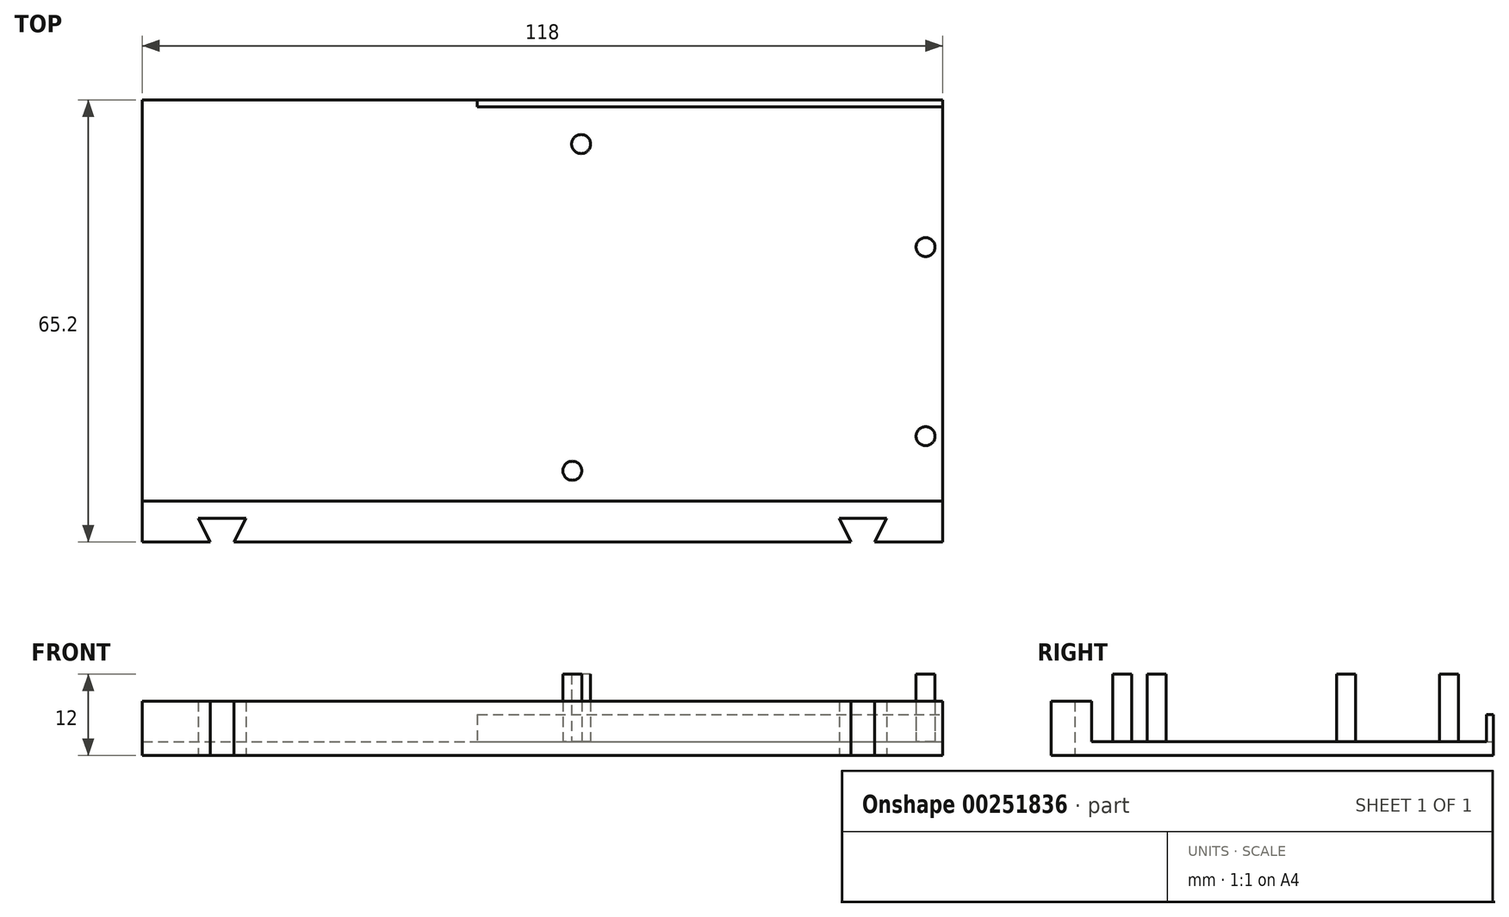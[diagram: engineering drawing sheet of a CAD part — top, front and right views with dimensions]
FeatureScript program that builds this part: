
annotation { "Feature Type Name" : "Feature", "Feature Type Description" : "" }
export const myFeature = defineFeature(function(context is Context, id is Id, definition is map)
    precondition{}
    {
        {
            var Q0;
            Q0=qCreatedBy(makeId("Top.planeOp"),FACE);
            var sketch = newSketch(context, id + "F0", { "sketchPlane" : qUnion([Q0])});
            skLineSegment(sketch, "E0", {"start": v(-10, 20) * mm, "end": v(-10, 0) * mm, "construction": true});
            skLineSegment(sketch, "E1", {"start": v(-10, 0) * mm, "end": v(-10, -10) * mm, "construction": true});
            skLineSegment(sketch, "E2", {"start": v(-10, -10) * mm, "end": v(0, -10) * mm, "construction": true});
            skLineSegment(sketch, "E3", {"start": v(0, -10) * mm, "end": v(100, -10) * mm, "construction": true});
            skLineSegment(sketch, "E4.bottom", {"start": v(100, 73.2) * mm, "end": v(168.6, 73.2) * mm});
            skLineSegment(sketch, "E4.top", {"start": v(100, 20) * mm, "end": v(168.6, 20) * mm});
            skLineSegment(sketch, "E4.left", {"start": v(100, 73.2) * mm, "end": v(100, 20) * mm});
            skLineSegment(sketch, "E4.right", {"start": v(168.6, 73.2) * mm, "end": v(168.6, 20) * mm});
            skLineSegment(sketch, "E5", {"start": v(115.3, -10) * mm, "end": v(166.1, -10) * mm, "construction": true});
            skLineSegment(sketch, "E6", {"start": v(-10, 22.5) * mm, "end": v(-10, 27.6) * mm, "construction": true});
            skLineSegment(sketch, "E7", {"start": v(-10, 27.6) * mm, "end": v(-10, 55.5) * mm, "construction": true});
            skCircle(sketch, "E8", {"center": v(-10, -10) * mm, "radius": 1.4 * mm, "construction": true});
            skCircle(sketch, "E9", {"center": v(114, 22.5) * mm, "radius": 1.4 * mm});
            skCircle(sketch, "E10", {"center": v(115.3, 70.7) * mm, "radius": 1.4 * mm});
            skCircle(sketch, "E11", {"center": v(166.1, 27.6) * mm, "radius": 1.4 * mm});
            skCircle(sketch, "E12", {"center": v(166.1, 55.5) * mm, "radius": 1.4 * mm});
            skLineSegment(sketch, "E13", {"start": v(-10, 55.5) * mm, "end": v(-10, 70.7) * mm, "construction": true});
            skLineSegment(sketch, "E14", {"start": v(115.3, -10) * mm, "end": v(114, -10) * mm, "construction": true});
            skLineSegment(sketch, "E15", {"start": v(114, -10) * mm, "end": v(100, -10) * mm, "construction": true});
            skLineSegment(sketch, "E16", {"start": v(166.1, -10) * mm, "end": v(168.6, -10) * mm, "construction": true});
            skLineSegment(sketch, "E17", {"start": v(-10, 70.7) * mm, "end": v(-10, 73.2) * mm, "construction": true});
            skLineSegment(sketch, "E18", {"start": v(-10, 22.5) * mm, "end": v(-10, 20) * mm, "construction": true});
            skLineSegment(sketch, "E19", {"start": v(100, 73.2) * mm, "end": v(100, 76.2) * mm});
            skLineSegment(sketch, "E20", {"start": v(100, 76.2) * mm, "end": v(168.6, 76.2) * mm});
            skLineSegment(sketch, "E21", {"start": v(168.6, 76.2) * mm, "end": v(168.6, 73.2) * mm});
            skLineSegment(sketch, "E22", {"start": v(100, 76.2) * mm, "end": v(100, 77.2) * mm});
            skLineSegment(sketch, "E23", {"start": v(100, 77.2) * mm, "end": v(168.6, 77.2) * mm});
            skLineSegment(sketch, "E24", {"start": v(168.6, 77.2) * mm, "end": v(168.6, 76.2) * mm});
            skLineSegment(sketch, "E25", {"start": v(62.35, 15.5) * mm, "end": v(62.35, 12) * mm, "construction": true});
            skLineSegment(sketch, "E26", {"start": v(62.35, 15.5) * mm, "end": v(58.85, 15.5) * mm});
            skLineSegment(sketch, "E27", {"start": v(65.85, 15.5) * mm, "end": v(62.35, 15.5) * mm});
            skLineSegment(sketch, "E28", {"start": v(60.6, 12) * mm, "end": v(64.1, 12) * mm, "construction": true});
            skLineSegment(sketch, "E29", {"start": v(58.85, 15.5) * mm, "end": v(60.6, 12) * mm});
            skLineSegment(sketch, "E30", {"start": v(65.85, 15.5) * mm, "end": v(64.1, 12) * mm});
            skLineSegment(sketch, "E31", {"start": v(60.6, 12) * mm, "end": v(50.6, 12) * mm});
            skLineSegment(sketch, "E32", {"start": v(50.6, 12) * mm, "end": v(50.6, 18) * mm});
            skLineSegment(sketch, "E33", {"start": v(156.85, 15.5) * mm, "end": v(156.85, 12) * mm, "construction": true});
            skLineSegment(sketch, "E34", {"start": v(156.85, 15.5) * mm, "end": v(153.35, 15.5) * mm});
            skLineSegment(sketch, "E35", {"start": v(160.35, 15.5) * mm, "end": v(156.85, 15.5) * mm});
            skLineSegment(sketch, "E36", {"start": v(155.1, 12) * mm, "end": v(158.6, 12) * mm, "construction": true});
            skLineSegment(sketch, "E37", {"start": v(153.35, 15.5) * mm, "end": v(155.1, 12) * mm});
            skLineSegment(sketch, "E38", {"start": v(160.35, 15.5) * mm, "end": v(158.6, 12) * mm});
            skLineSegment(sketch, "E39", {"start": v(64.1, 12) * mm, "end": v(155.1, 12) * mm});
            skLineSegment(sketch, "E40", {"start": v(158.6, 12) * mm, "end": v(168.6, 12) * mm});
            skLineSegment(sketch, "E41", {"start": v(168.6, 12) * mm, "end": v(168.6, 18) * mm});
            skLineSegment(sketch, "E42", {"start": v(50.6, 18) * mm, "end": v(168.6, 18) * mm});
            skLineSegment(sketch, "E43", {"start": v(50.6, 18) * mm, "end": v(50.6, 20) * mm});
            skLineSegment(sketch, "E44", {"start": v(50.6, 20) * mm, "end": v(168.6, 20) * mm});
            skLineSegment(sketch, "E45", {"start": v(168.6, 20) * mm, "end": v(168.6, 18) * mm});
            skLineSegment(sketch, "E46", {"start": v(50.6, 20) * mm, "end": v(50.6, 77.2) * mm});
            skLineSegment(sketch, "E47", {"start": v(50.6, 77.2) * mm, "end": v(100, 77.2) * mm});
            skSolve(sketch);
        }
        {
            var Q0;
            Q0=makeQuery(id+"F0.imprint","IMPRINT",FACE,{"disambiguationData":[TD([[makeQuery(id+"F0.imprint","IMPRINT",EDGE,{"derivedFrom":sQuery(id+"F0.wireOp",EDGE,"E4.bottom")}),-1.0]])]});
            var Q1;
            Q1=makeQuery(id+"F0.imprint","IMPRINT",FACE,{"disambiguationData":[TD([[makeQuery(id+"F0.imprint","IMPRINT",EDGE,{"derivedFrom":sQuery(id+"F0.wireOp",EDGE,"E4.bottom")}),1.0]])]});
            var Q2;
            Q2=makeQuery(id+"F0.imprint","IMPRINT",FACE,{"disambiguationData":[TD([[makeQuery(id+"F0.imprint","IMPRINT",EDGE,{"derivedFrom":sQuery(id+"F0.wireOp",EDGE,"E42")}),1.0]])]});
            var Q3;
            {var subQ1=sQuery(id+"F0.wireOp",EDGE,"E4.left");Q3=makeQuery(id+"F0.imprint","IMPRINT",FACE,{"disambiguationData":[TD([[makeQuery(id+"F0.imprint","IMPRINT",EDGE,{"derivedFrom":subQ1}),-1.0]])]});}
            extrude(context, id + "F1", {"entities" : qUnion([Q0, Q1, Q2, Q3]), "depth" : 2 * mm});
        }
        {
            var Q0;
            Q0=makeQuery(id+"F0.imprint","IMPRINT",FACE,{"disambiguationData":[TD([[makeQuery(id+"F0.imprint","IMPRINT",EDGE,{"derivedFrom":sQuery(id+"F0.wireOp",EDGE,"E10")}),1.0]])]});
            var Q1;
            Q1=makeQuery(id+"F0.imprint","IMPRINT",FACE,{"disambiguationData":[TD([[makeQuery(id+"F0.imprint","IMPRINT",EDGE,{"derivedFrom":sQuery(id+"F0.wireOp",EDGE,"E12")}),1.0]])]});
            var Q2;
            Q2=makeQuery(id+"F0.imprint","IMPRINT",FACE,{"disambiguationData":[TD([[makeQuery(id+"F0.imprint","IMPRINT",EDGE,{"derivedFrom":sQuery(id+"F0.wireOp",EDGE,"E11")}),1.0]])]});
            var Q3;
            Q3=makeQuery(id+"F0.imprint","IMPRINT",FACE,{"disambiguationData":[TD([[makeQuery(id+"F0.imprint","IMPRINT",EDGE,{"derivedFrom":sQuery(id+"F0.wireOp",EDGE,"E9")}),1.0]])]});
            extrude(context, id + "F2", {"entities" : qUnion([Q0, Q1, Q2, Q3]), "operationType" : NewBodyOperationType.ADD, "depth" : 12 * mm});
        }
        {
            var Q0;
            Q0=makeQuery(id+"F0.imprint","IMPRINT",FACE,{"disambiguationData":[TD([[makeQuery(id+"F0.imprint","IMPRINT",EDGE,{"derivedFrom":sQuery(id+"F0.wireOp",EDGE,"E20")}),1.0]])]});
            extrude(context, id + "F3", {"entities" : qUnion([Q0]), "operationType" : NewBodyOperationType.ADD, "depth" : 6 * mm});
        }
        {
            var Q0;
            Q0=makeQuery(id+"F0.imprint","IMPRINT",FACE,{"disambiguationData":[TD([[makeQuery(id+"F0.imprint","IMPRINT",EDGE,{"derivedFrom":sQuery(id+"F0.wireOp",EDGE,"E26")}),-1.0]])]});
            extrude(context, id + "F4", {"entities" : qUnion([Q0]), "operationType" : NewBodyOperationType.ADD, "depth" : 8 * mm});
        }
    });
